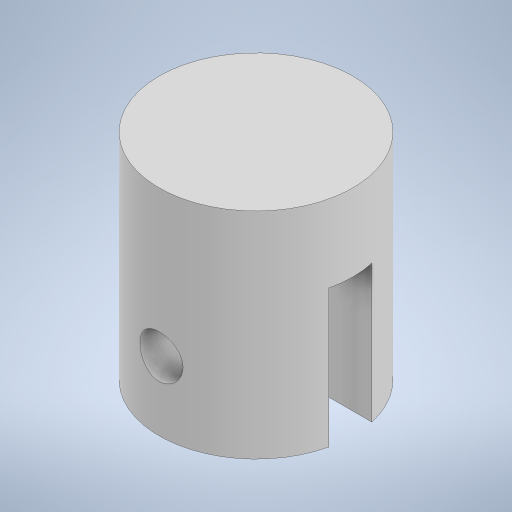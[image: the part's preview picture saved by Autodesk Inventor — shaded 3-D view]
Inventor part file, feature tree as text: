
AUTODESK INVENTOR PART (.ipt)
format: ipt  version: 2023 (Build 270158000, 158)  size: 219,648 bytes
history: native  units: in
note: dims shown in document units (in); Inventor stores cm internally (conversion verified against a paired STEP export)
features: extrude x3, sketch x2
ambient origin geometry x8: Origin, YZ Plane, XZ Plane, XY Plane, X Axis, Y Axis, Z Axis, Center Point
bodies: Solid1 (feature_tree)
feature tree (5):
  sketch  "Sketch1"  dims[d1=0.1406in d2=0.1875in]
  extrude  "Extrusion1"  Depth=0.1875in
  extrude  "Extrusion2"  Depth=0.0312in
  extrude  "Extrusion3"  Depth=0.0312in TaperAngle=0.0deg
  sketch  "Sketch2"  dims[d3=0.0156in d4=0.0312in d5=0.156in d6=0.0in d7=0.1in d8=0.0in d9=0.0312in d10=0.05in d11=1.0in d12=0.0in]
